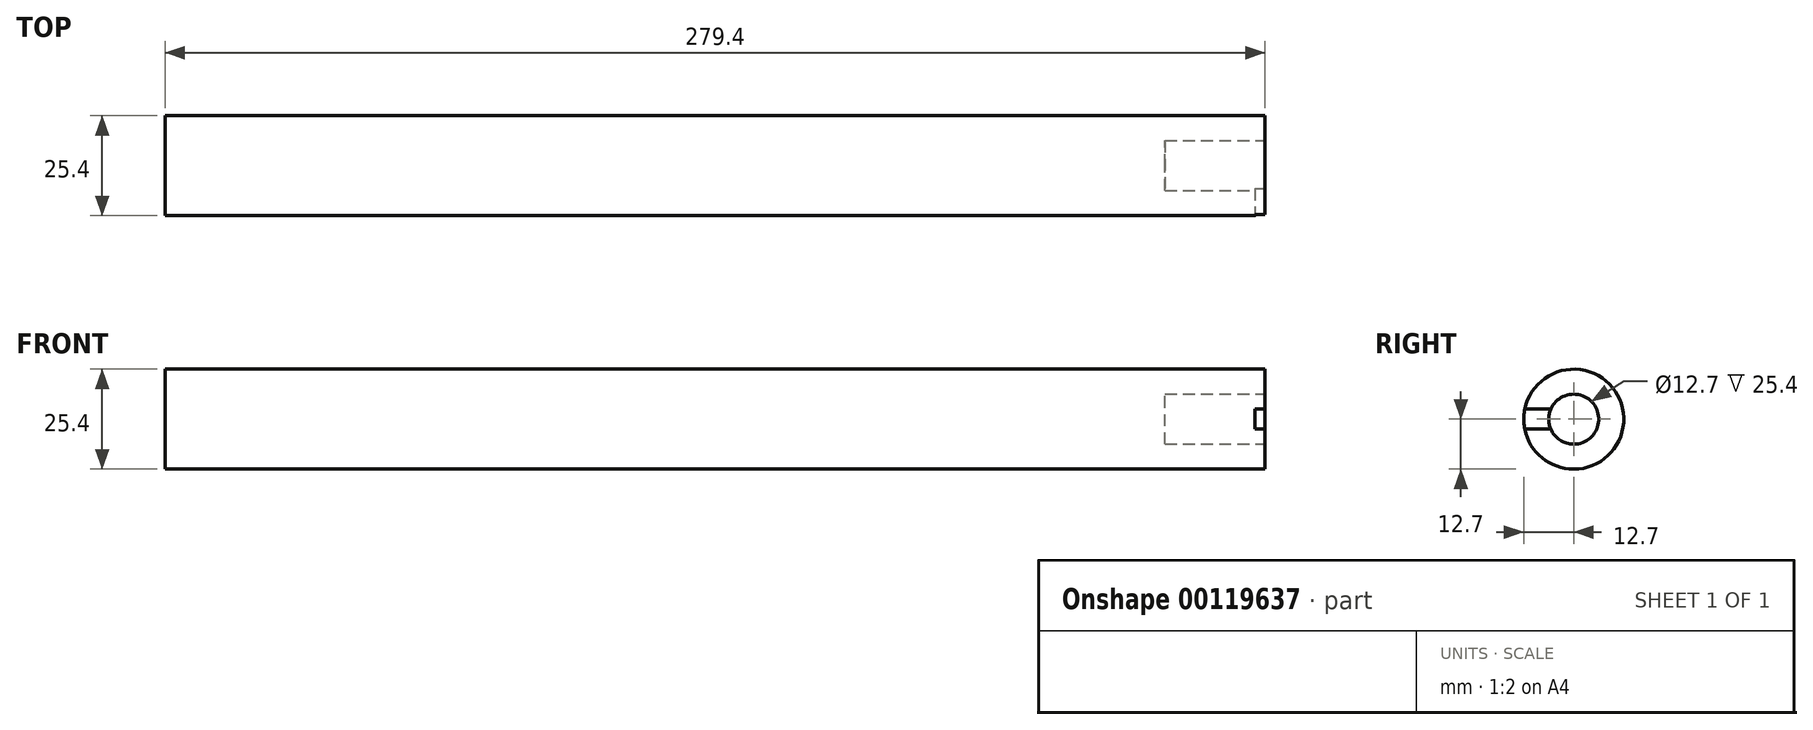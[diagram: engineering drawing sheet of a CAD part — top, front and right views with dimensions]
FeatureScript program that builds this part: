
annotation { "Feature Type Name" : "Feature", "Feature Type Description" : "" }
export const myFeature = defineFeature(function(context is Context, id is Id, definition is map)
    precondition{}
    {
        {
            var Q0;
            Q0=qCreatedBy(makeId("Right.planeOp"),FACE);
            var sketch = newSketch(context, id + "F0", { "sketchPlane" : qUnion([Q0])});
            skCircle(sketch, "E0", {"center": v(0, 0) * mm, "radius": 12.7 * mm});
            skSolve(sketch);
        }
        {
            var Q0;
            Q0 = qSketchRegion(id + "F0", true);
            extrude(context, id + "F1", {"entities" : qUnion([Q0]), "oppositeDirection" : true, "depth" : 279.4 * mm});
        }
        {
            var Q0;
            Q0=makeQuery(id+"F1.opExtrude","CAP_FACE",FACE,{"disambiguationData":[OSD([sQuery(id+"F0.wireOp",EDGE,"E0")])],"isStart":true});
            var sketch = newSketch(context, id + "F2", { "sketchPlane" : qUnion([Q0])});
            skCircle(sketch, "E1", {"center": v(0, 0) * mm, "radius": 6.35 * mm});
            skSolve(sketch);
        }
        {
            var Q0;
            Q0 = qSketchRegion(id + "F2", true);
            extrude(context, id + "F3", {"entities" : qUnion([Q0]), "operationType" : NewBodyOperationType.REMOVE, "oppositeDirection" : true, "depth" : 25.4 * mm});
        }
        {
            var Q0;
            Q0=makeQuery(id+"F1.opExtrude","CAP_FACE",FACE,{"disambiguationData":[OSD([sQuery(id+"F0.wireOp",EDGE,"E0")])],"isStart":true});
            var sketch = newSketch(context, id + "F4", { "sketchPlane" : qUnion([Q0])});
            skLineSegment(sketch, "E2", {"start": v(0, 0) * mm, "end": v(0, 2.54) * mm});
            skLineSegment(sketch, "E3", {"start": v(0, 2.54) * mm, "end": v(-12.44, 2.54) * mm});
            skLineSegment(sketch, "E4", {"start": v(0, 0) * mm, "end": v(0, -2.54) * mm});
            skLineSegment(sketch, "E5", {"start": v(0, -2.54) * mm, "end": v(-12.44, -2.54) * mm});
            skArc(sketch, "E6", {"start": v(-12.44, 2.54) * mm, "mid": v(-12.7, 0) * mm, "end": v(-12.44, -2.54) * mm});
            skSolve(sketch);
        }
        {
            var Q0;
            {var subQ0=sQuery(id+"F4.wireOp",EDGE,"E6");Q0=makeQuery(id+"F4.imprint","IMPRINT",FACE,{"disambiguationData":[TD([[makeQuery(id+"F4.imprint","IMPRINT",EDGE,{"derivedFrom":subQ0}),1.0]])]});}
            var Q1;
            {var subQ0=sQuery(id+"FL3gcKpaCdp7nZU_1.3.F4.wireOp",EDGE,"E6");Q1=makeQuery(id+"FL3gcKpaCdp7nZU_1.3.F4.imprint","IMPRINT",FACE,{"disambiguationData":[TD([[makeQuery(id+"FL3gcKpaCdp7nZU_1.3.F4.imprint","IMPRINT",EDGE,{"derivedFrom":subQ0}),1.0]])]});}
            var Q2;
            {var subQ0=sQuery(id+"FL3gcKpaCdp7nZU_1.1.F4.wireOp",EDGE,"E6");Q2=makeQuery(id+"FL3gcKpaCdp7nZU_1.1.F4.imprint","IMPRINT",FACE,{"disambiguationData":[TD([[makeQuery(id+"FL3gcKpaCdp7nZU_1.1.F4.imprint","IMPRINT",EDGE,{"derivedFrom":subQ0}),1.0]])]});}
            var Q3;
            {var subQ0=sQuery(id+"FL3gcKpaCdp7nZU_1.2.F4.wireOp",EDGE,"E6");Q3=makeQuery(id+"FL3gcKpaCdp7nZU_1.2.F4.imprint","IMPRINT",FACE,{"disambiguationData":[TD([[makeQuery(id+"FL3gcKpaCdp7nZU_1.2.F4.imprint","IMPRINT",EDGE,{"derivedFrom":subQ0}),1.0]])]});}
            var Q4;
            Q4=sQuery(id+"FL3gcKpaCdp7nZU_1.3.F4.wireOp",EDGE,"E5");
            var Q5;
            Q5=sQuery(id+"FL3gcKpaCdp7nZU_1.1.F4.wireOp",EDGE,"E2");
            var Q6;
            Q6=sQuery(id+"FL3gcKpaCdp7nZU_1.1.F4.wireOp",EDGE,"E4");
            var Q7;
            Q7=sQuery(id+"FL3gcKpaCdp7nZU_1.3.F4.wireOp",EDGE,"E3");
            var Q8;
            Q8=sQuery(id+"FL3gcKpaCdp7nZU_1.3.F4.wireOp",EDGE,"E6");
            extrude(context, id + "F5", {"entities" : qUnion([Q0, Q1, Q2, Q3]), "operationType" : NewBodyOperationType.REMOVE, "surfaceEntities" : qUnion([Q4, Q5, Q6, Q7, Q8]), "oppositeDirection" : true, "depth" : 2.54 * mm});
        }
    });
